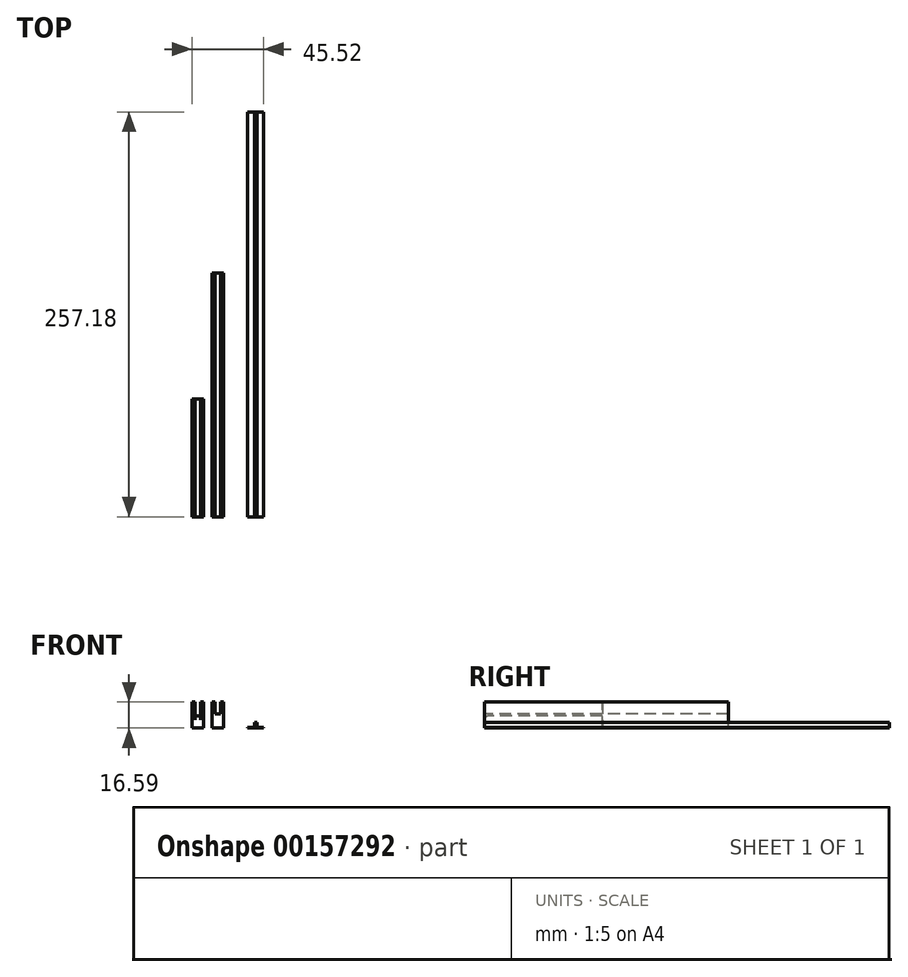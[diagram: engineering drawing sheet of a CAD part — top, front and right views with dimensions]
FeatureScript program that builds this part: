
annotation { "Feature Type Name" : "Feature", "Feature Type Description" : "" }
export const myFeature = defineFeature(function(context is Context, id is Id, definition is map)
    precondition{}
    {
        {
            var Q0;
            Q0=qCreatedBy(makeId("Front.planeOp"),FACE);
            var sketch = newSketch(context, id + "F0", { "sketchPlane" : qUnion([Q0])});
            skLineSegment(sketch, "E0", {"start": v(-12.7, 0) * mm, "end": v(-12.7, 16.51) * mm});
            skLineSegment(sketch, "E1", {"start": v(-12.7, 16.51) * mm, "end": v(-14.73, 16.51) * mm});
            skLineSegment(sketch, "E2", {"start": v(-14.73, 16.51) * mm, "end": v(-14.73, 8.9) * mm});
            skLineSegment(sketch, "E3", {"start": v(-14.73, 8.9) * mm, "end": v(-18.08, 8.9) * mm});
            skLineSegment(sketch, "E4", {"start": v(-18.08, 8.9) * mm, "end": v(-18.08, 16.51) * mm});
            skLineSegment(sketch, "E5", {"start": v(-18.08, 16.51) * mm, "end": v(-20.12, 16.51) * mm});
            skLineSegment(sketch, "E6", {"start": v(-20.12, 16.51) * mm, "end": v(-20.12, 0) * mm});
            skLineSegment(sketch, "E7", {"start": v(-20.12, 0) * mm, "end": v(-12.7, 0) * mm});
            skSolve(sketch);
        }
        {
            var Q0;
            Q0 = qSketchRegion(id + "F0", true);
            extrude(context, id + "F1", {"entities" : qUnion([Q0]), "oppositeDirection" : true, "depth" : 154.94 * mm});
        }
        {
            var Q0;
            Q0=qCreatedBy(makeId("Front.planeOp"),FACE);
            var sketch = newSketch(context, id + "F2", { "sketchPlane" : qUnion([Q0])});
            skLineSegment(sketch, "E8", {"start": v(-25.4, 0) * mm, "end": v(-25.4, 16.51) * mm});
            skLineSegment(sketch, "E9", {"start": v(-25.4, 16.51) * mm, "end": v(-27.43, 16.51) * mm});
            skLineSegment(sketch, "E10", {"start": v(-27.43, 16.51) * mm, "end": v(-27.43, 7.7) * mm});
            skLineSegment(sketch, "E11", {"start": v(-27.43, 7.7) * mm, "end": v(-30.78, 7.7) * mm});
            skLineSegment(sketch, "E12", {"start": v(-30.78, 7.7) * mm, "end": v(-30.78, 16.59) * mm});
            skLineSegment(sketch, "E13", {"start": v(-30.78, 16.59) * mm, "end": v(-32.82, 16.59) * mm});
            skLineSegment(sketch, "E14", {"start": v(-32.82, 16.59) * mm, "end": v(-32.82, 0) * mm});
            skLineSegment(sketch, "E15", {"start": v(-32.82, 0) * mm, "end": v(-25.4, 0) * mm});
            skSolve(sketch);
        }
        {
            var Q0;
            Q0 = qSketchRegion(id + "F2", true);
            extrude(context, id + "F3", {"entities" : qUnion([Q0]), "oppositeDirection" : true, "depth" : 74.93 * mm});
        }
        {
            var Q0;
            Q0=makeQuery(id+"F3.opExtrude","CAP_EDGE",EDGE,{"disambiguationData":[OSD([sQuery(id+"F2.wireOp",EDGE,"E11")])],"isStart":true});
            fillet(context, id + "F4", {"entities" : qUnion([Q0]), "radius" : 2.54 * mm, "tangentPropagation" : true, "allowEdgeOverflow" : false});
        }
        {
            var Q0;
            Q0=qCreatedBy(makeId("Front.planeOp"),FACE);
            var sketch = newSketch(context, id + "F5", { "sketchPlane" : qUnion([Q0])});
            skLineSegment(sketch, "E16", {"start": v(2.54, 0) * mm, "end": v(2.54, 0.4) * mm});
            skLineSegment(sketch, "E17", {"start": v(2.54, 0.4) * mm, "end": v(6.86, 0.4) * mm});
            skLineSegment(sketch, "E18", {"start": v(6.86, 0.4) * mm, "end": v(6.86, 3.45) * mm});
            skLineSegment(sketch, "E19", {"start": v(6.86, 3.45) * mm, "end": v(8.38, 3.45) * mm});
            skLineSegment(sketch, "E20", {"start": v(8.38, 3.45) * mm, "end": v(8.38, 0.4) * mm});
            skLineSegment(sketch, "E21", {"start": v(8.38, 0.4) * mm, "end": v(12.7, 0.4) * mm});
            skLineSegment(sketch, "E22", {"start": v(12.7, 0.4) * mm, "end": v(12.7, 0) * mm});
            skLineSegment(sketch, "E23", {"start": v(12.7, 0) * mm, "end": v(2.54, 0) * mm});
            skSolve(sketch);
        }
        {
            var Q0;
            Q0 = qSketchRegion(id + "F5", true);
            extrude(context, id + "F6", {"entities" : qUnion([Q0]), "oppositeDirection" : true, "depth" : 257.18 * mm});
        }
    });
